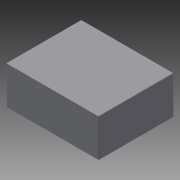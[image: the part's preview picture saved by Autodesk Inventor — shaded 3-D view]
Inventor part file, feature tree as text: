
AUTODESK INVENTOR PART (.ipt)
format: ipt  version: 2016 SP1 (Build 200210100, 210)  size: 89,600 bytes
history: native  units: in
note: dims shown in document units (in); Inventor stores cm internally (conversion verified against a paired STEP export)
features: reference x3, extrude x1, fillet x1, sketch x1
ambient origin geometry x8: Origin, YZ Plane, XZ Plane, XY Plane, X Axis, Y Axis, Z Axis, Center Point
bodies: Solid1 (feature_tree)
feature tree (6):
  extrude  "Extrusion1"  Depth=2.97in
  fillet  "Fillet1"  Radius=5.74in
  sketch  "Sketch1"  dims[d0=7.07in d1=2.97in d2=5.74in d3=0.0in d4=0.05in]
  reference  "Reference1"
  reference  "Reference2"
  reference  "Reference3"
